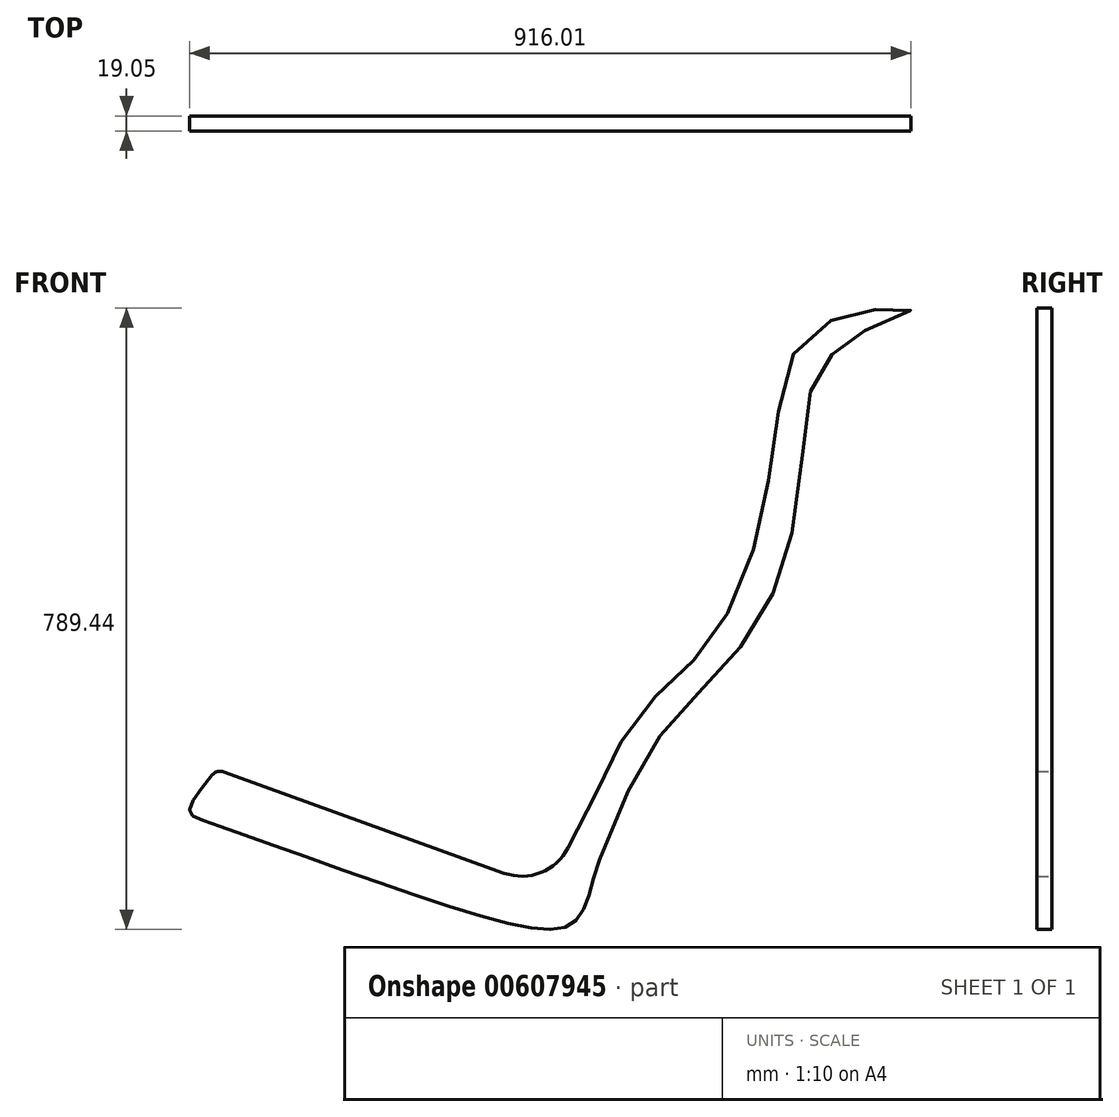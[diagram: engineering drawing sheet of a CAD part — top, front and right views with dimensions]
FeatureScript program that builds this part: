
annotation { "Feature Type Name" : "Feature", "Feature Type Description" : "" }
export const myFeature = defineFeature(function(context is Context, id is Id, definition is map)
    precondition{}
    {
        {
            var Q0;
            Q0=qCreatedBy(makeId("Front.planeOp"),FACE);
            var sketch = newSketch(context, id + "F0", { "sketchPlane" : qUnion([Q0])});
            skLineSegment(sketch, "E0", {"start": v(-298.71, 168.23) * mm, "end": v(356.96, 89.37) * mm, "construction": true});
            skLineSegment(sketch, "E1", {"start": v(-305.36, 41.9) * mm, "end": v(51.35, -86.79) * mm});
            skArc(sketch, "E2", {"start": v(51.35, -86.79) * mm, "mid": v(98.03, -86.04) * mm, "end": v(132.5, -54.55) * mm});
            skFitSpline(sketch, "E3", {"points": [v(132.5, -54.55) * mm, v(174.97, 29.68) * mm, v(209.84, 96.52) * mm, v(264.06, 158.07) * mm, v(309.72, 203.4) * mm, v(358.68, 296.21) * mm, v(387.77, 416.08) * mm, v(405.02, 528.86) * mm, v(434.3, 594.77) * mm, v(490.06, 623.02) * mm, v(538.27, 630.25) * mm, v(567.87, 628.96) * mm, v(518.03, 606.23) * mm, v(480.95, 583.82) * mm, v(450.17, 550.8) * mm, v(435.46, 493.32) * mm, v(417.48, 349.74) * mm, v(386.58, 256.25) * mm, v(329.8, 174.21) * mm, v(268.39, 111.31) * mm, v(218.9, 36.45) * mm, v(167.71, -84.56) * mm, v(138.7, -150.27) * mm, v(11.93, -138.34) * mm, v(-320.17, -23.53) * mm, v(-348.14, -6.74) * mm, v(-313.7, 44.9) * mm], "startDerivative": vector(1105.47, 2132.24) * mm, "endDerivative": vector(1571.17, 1863.8) * mm, "construction": true});
            skArc(sketch, "E4.filletArc", {"start": v(-305.36, 41.9) * mm, "mid": v(-312.98, 42.22) * mm, "end": v(-319.4, 38.1) * mm});
            skFitSpline(sketch, "E5", {"points": [v(132.5, -54.55) * mm, v(174.97, 29.68) * mm, v(209.84, 96.52) * mm, v(264.06, 158.07) * mm, v(309.72, 203.4) * mm, v(358.68, 296.21) * mm, v(387.77, 416.08) * mm, v(405.02, 528.86) * mm, v(434.3, 594.77) * mm, v(490.06, 623.02) * mm, v(538.27, 630.25) * mm, v(567.87, 628.96) * mm, v(518.03, 606.23) * mm, v(480.95, 583.82) * mm, v(450.17, 550.8) * mm, v(435.46, 493.32) * mm, v(417.48, 349.74) * mm, v(386.58, 256.25) * mm, v(329.8, 174.21) * mm, v(268.39, 111.31) * mm, v(218.9, 36.45) * mm, v(167.71, -84.56) * mm, v(138.7, -150.27) * mm, v(11.93, -138.34) * mm, v(-320.17, -23.53) * mm, v(-348.14, -6.74) * mm, v(-313.7, 44.9) * mm], "startDerivative": vector(1105.47, 2132.24) * mm, "endDerivative": vector(1571.17, 1863.8) * mm});
            skLineSegment(sketch, "E6", {"start": v(132.5, -54.55) * mm, "end": v(172.45, -69.93) * mm});
            skSolve(sketch);
        }
        {
            var Q0;
            Q0 = qSketchRegion(id + "F0", true);
            extrude(context, id + "F1", {"entities" : qUnion([Q0]), "depth" : 19.05 * mm, "offsetDistance" : 25.4 * mm});
        }
    });
